# Revit family: Common_Vent-Navien-Collar_Kit
name_source: partatom
category: Mechanical Equipment
revit_build: Autodesk Revit 2017 (Build: 20160225_1515(x64)
units: mm (PartAtom-declared; Revit-internal decimal feet)

## family parameters
Always vertical = Yes
Cut with Voids When Loaded = No
OmniClass Number = 23.75.70.11.14.14
OmniClass Title = Dampers for Air Ductwork
Part Type = Normal
Room Calculation Point = No
Round Connector Dimension = Use Diameter
Shared = No
Work Plane-Based = Yes

## types (1)
- Common Vent Collar Kit
    Default Elevation = 1219 mm
    Depth = 137 mm  [stored 0.449475 ft]
    Description = The Navien backflow damper prevents backflow (back-draft) at the exhaust vent while the water heater or boiler unit operates.
    Finish = Plastic - Navien - White
    Height = 201 mm  [stored 0.659449 ft]
    Inlet = 76 mm
    Installation Type = Duct Fitting
    Manufacturer = Navien, Inc.
    Manufacturer Fax Number = (949) 420-0430
    Model = Contact Navien for Product Documentation
    Outlet = 76 mm
    Product Documentation Link = Contact Navien for Product Documentation
    Product Name = Common Vent Collar Kit
    Product Page URL = https://www.navieninc.com
    URL = https://www.navieninc.com
    Version = 2017 - v1.0.a
    Weight = 0.00 lbf
    Width = 137 mm  [stored 0.449475 ft]

note: [stored X ft] marks values corroborated as IEEE doubles in the binary element streams (Revit-internal decimal feet)

## geometry (parser evidence)
native form markers: Sweep x2
no freeform markers — native parametric forms only
